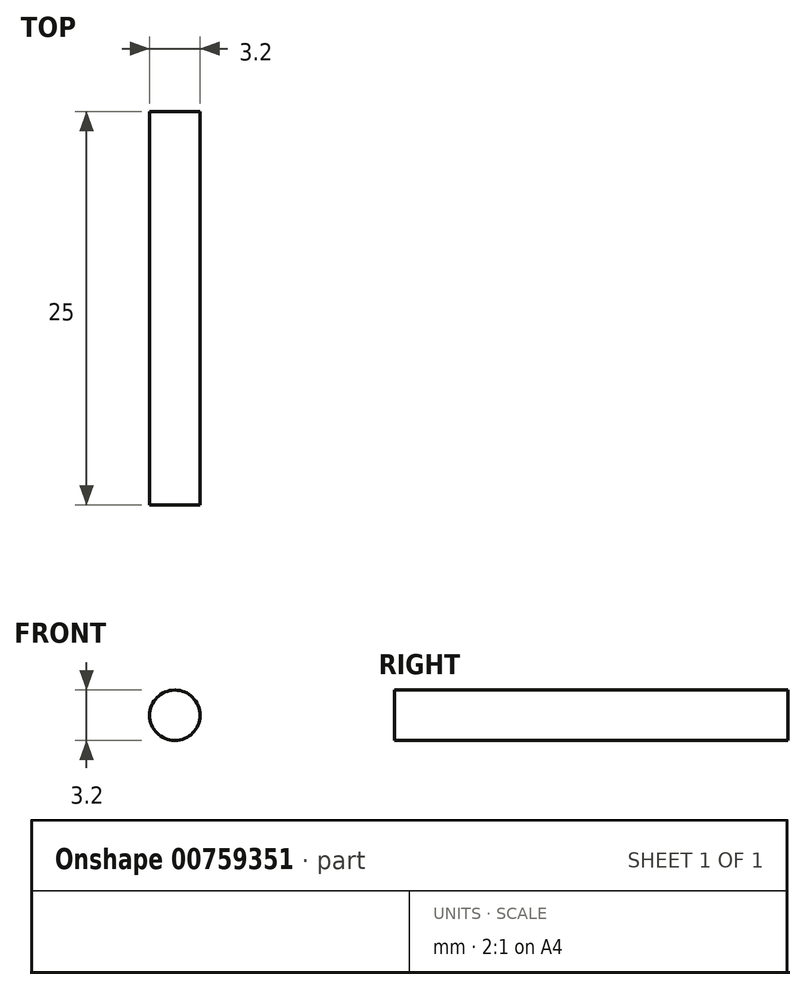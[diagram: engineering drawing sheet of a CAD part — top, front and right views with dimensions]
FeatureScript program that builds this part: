
annotation { "Feature Type Name" : "Feature", "Feature Type Description" : "" }
export const myFeature = defineFeature(function(context is Context, id is Id, definition is map)
    precondition{}
    {
        {
            var Q0;
            Q0=qCreatedBy(makeId("Front.planeOp"),FACE);
            var sketch = newSketch(context, id + "F0", { "sketchPlane" : qUnion([Q0])});
            skCircle(sketch, "E0", {"center": v(0, 0) * mm, "radius": 1.6 * mm});
            skSolve(sketch);
        }
        {
            var Q0;
            Q0=makeQuery(id+"F0.imprint","IMPRINT",FACE,{"disambiguationData":[TD([[makeQuery(id+"F0.imprint","IMPRINT",EDGE,{"derivedFrom":sQuery(id+"F0.wireOp",EDGE,"E0")}),1.0]])]});
            extrude(context, id + "F1", {"entities" : qUnion([Q0]), "depth" : 25 * mm, "offsetDistance" : 25 * mm});
        }
    });
